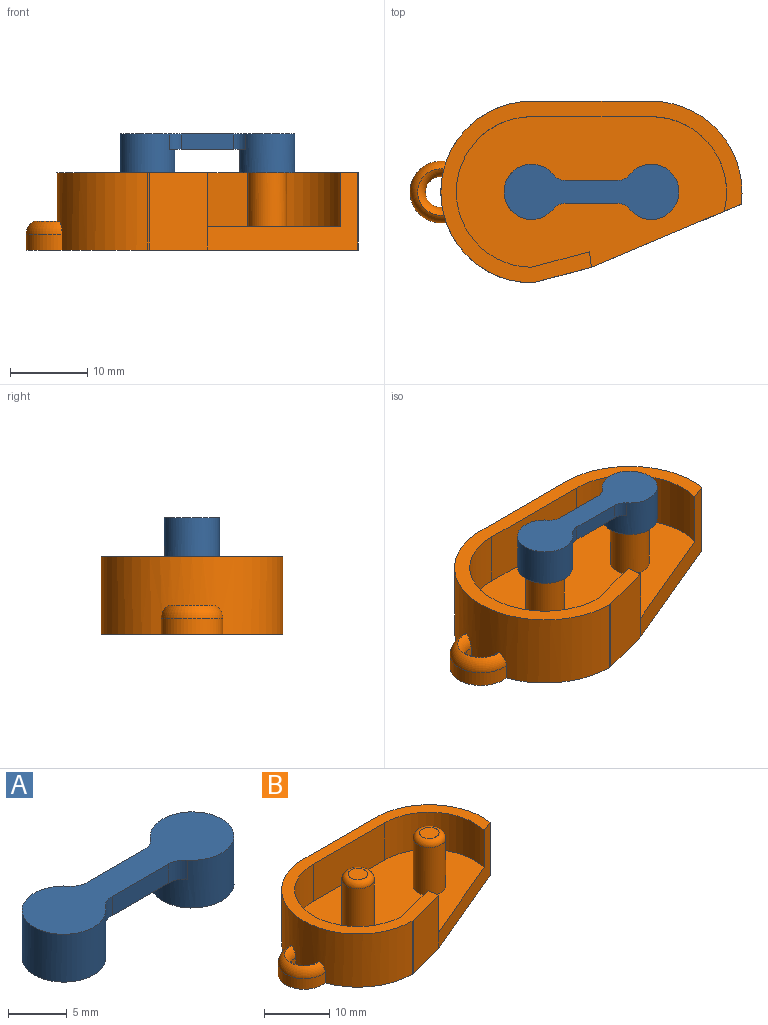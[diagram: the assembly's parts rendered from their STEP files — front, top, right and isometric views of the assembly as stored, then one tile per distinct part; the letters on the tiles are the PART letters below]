
ASSEMBLY  parts=2 mates=1
PART A: 16 faces, bbox 22.7x7.2x5 mm
  f0: cylinder r=3.58mm len=7.15mm, axis (0,0,-1), area 102.7mm2, adj f4,f5,f7,f12,f13
  f1: plane 6.79x2mm, normal (0,-1,0), area 13.6mm2, adj f4,f5,f12,f14
  f2: cylinder r=3.58mm len=7.15mm, axis (0,0,-1), area 102.7mm2, adj f4,f5,f10,f14,f15
  f3: plane 6.79x2mm, normal (0,1,0), area 13.6mm2, adj f4,f5,f13,f15
  f4: plane 22.65x7.15mm, normal (0,0,1), area 106.3mm2, adj f0,f1,f2,f3,f12,f13,f14,f15
  f5: plane 9.92x4.47mm, normal (0,0,-1), area 26mm2, adj f0,f1,f2,f3,f12,f13,f14,f15
  f6: cylinder r=2.58mm len=5.15mm, axis (0,0,1), area 48.5mm2, adj f7,f8
  f7: plane 7.15x7.15mm, normal (0,0,-1), area 19.3mm2, adj f0,f6
  f8: plane 5.15x5.15mm, normal (0,0,-1), area 20.8mm2, adj f6
  f9: cylinder r=2.58mm len=5.15mm, axis (0,0,1), area 48.5mm2, adj f10,f11
  f10: plane 7.15x7.15mm, normal (0,0,-1), area 19.3mm2, adj f2,f9
  f11: plane 5.15x5.15mm, normal (0,0,-1), area 20.8mm2, adj f9
  f12: cylinder r=2mm len=2mm, axis (0,0,-1), area 3.6mm2, adj f0,f1,f4,f5
  f13: cylinder r=2mm len=2mm, axis (0,0,-1), area 3.6mm2, adj f0,f3,f4,f5
  f14: cylinder r=2mm len=2mm, axis (0,0,-1), area 3.6mm2, adj f1,f2,f4,f5
  f15: cylinder r=2mm len=2mm, axis (0,0,-1), area 3.6mm2, adj f2,f3,f4,f5
PART B: 24 faces, bbox 43.3x23.5x13 mm
  f0: cylinder r=11.75mm len=23.5mm, axis (0,0,-1), area 356.1mm2, adj f6,f7,f11,f12,f14,f15,f16,f17
  f1: plane 15.5x7mm, normal (0,-1,0), area 108.5mm2, adj f2,f3,f11,f13
  f2: cylinder r=9.75mm len=19.5mm, axis (0,0,-1), area 214.4mm2, adj f1,f10,f11,f13
  f3: cylinder r=9.75mm len=12.25mm, axis (0,0,-1), area 124.9mm2, adj f1,f4,f11,f13
  f4: plane 19.4x10mm, normal (0.39,-0.92,0), area 80mm2, adj f3,f5,f8,f11,f12,f13
  f5: cylinder r=11.75mm len=13.32mm, axis (0,0,-1), area 200.3mm2, adj f4,f6,f11,f12
  f6: plane 15.5x10mm, normal (0,1,0), area 155mm2, adj f0,f5,f11,f12
  f7: plane 10x0.26mm, normal (0,-1,0), area 2.6mm2, adj f0,f8,f11,f12
  f8: plane 10x7.49mm, normal (0.26,-0.97,0), area 77.5mm2, adj f4,f7,f9,f11,f12
  f9: plane 7x2mm, normal (0.99,0.13,0), area 14.1mm2, adj f8,f10,f11,f13
  f10: plane 7.49x7mm, normal (-0.26,0.97,0), area 54.2mm2, adj f2,f9,f11,f13
  f11: plane 39x23.5mm, normal (0,0,1), area 152.2mm2, adj f0,f1,f2,f3,f4,f5,f6,f7
  f12: plane 43x23.5mm, normal (0,0,-1), area 721.3mm2, adj f0,f4,f5,f6,f7,f8,f14,f15
  f13: plane 35x19.5mm, normal (0,0,1), area 509.4mm2, adj f1,f2,f3,f4,f9,f10,f18,f20
  f14: cylinder r=4mm len=8mm, axis (0,0,-1), area 27.9mm2, adj f0,f12,f17
  f15: cylinder r=2mm len=4mm, axis (0,0,-1), area 13.2mm2, adj f0,f12,f16
  f16: torus R=4mm, axis (0,0,1), area 16.4mm2, adj f0,f15,f17
  f17: torus R=2mm, axis (0,0,1), area 26.4mm2, adj f0,f14,f16
  f18: cylinder r=2.5mm len=9mm, axis (0,0,-1), area 141.4mm2, adj f13,f23
  f19: plane 3x3mm, normal (0,0,1), area 7.1mm2, adj f23
  f20: cylinder r=2.5mm len=9mm, axis (0,0,-1), area 141.4mm2, adj f13,f22
  f21: plane 3x3mm, normal (0,0,1), area 7.1mm2, adj f22
  f22: torus R=1.5mm, axis (0,0,1), area 21.1mm2, adj f20,f21
  f23: torus R=1.5mm, axis (0,0,1), area 21.1mm2, adj f18,f19
PLACE A t=(-4.27,1.97,8.84)mm
PLACE B t=(-4.27,1.97,-4.19)mm
MATE slider A.f0 <-> B.f0  axis (0,0,-1) through (-12.02,1.97,8.34)mm
